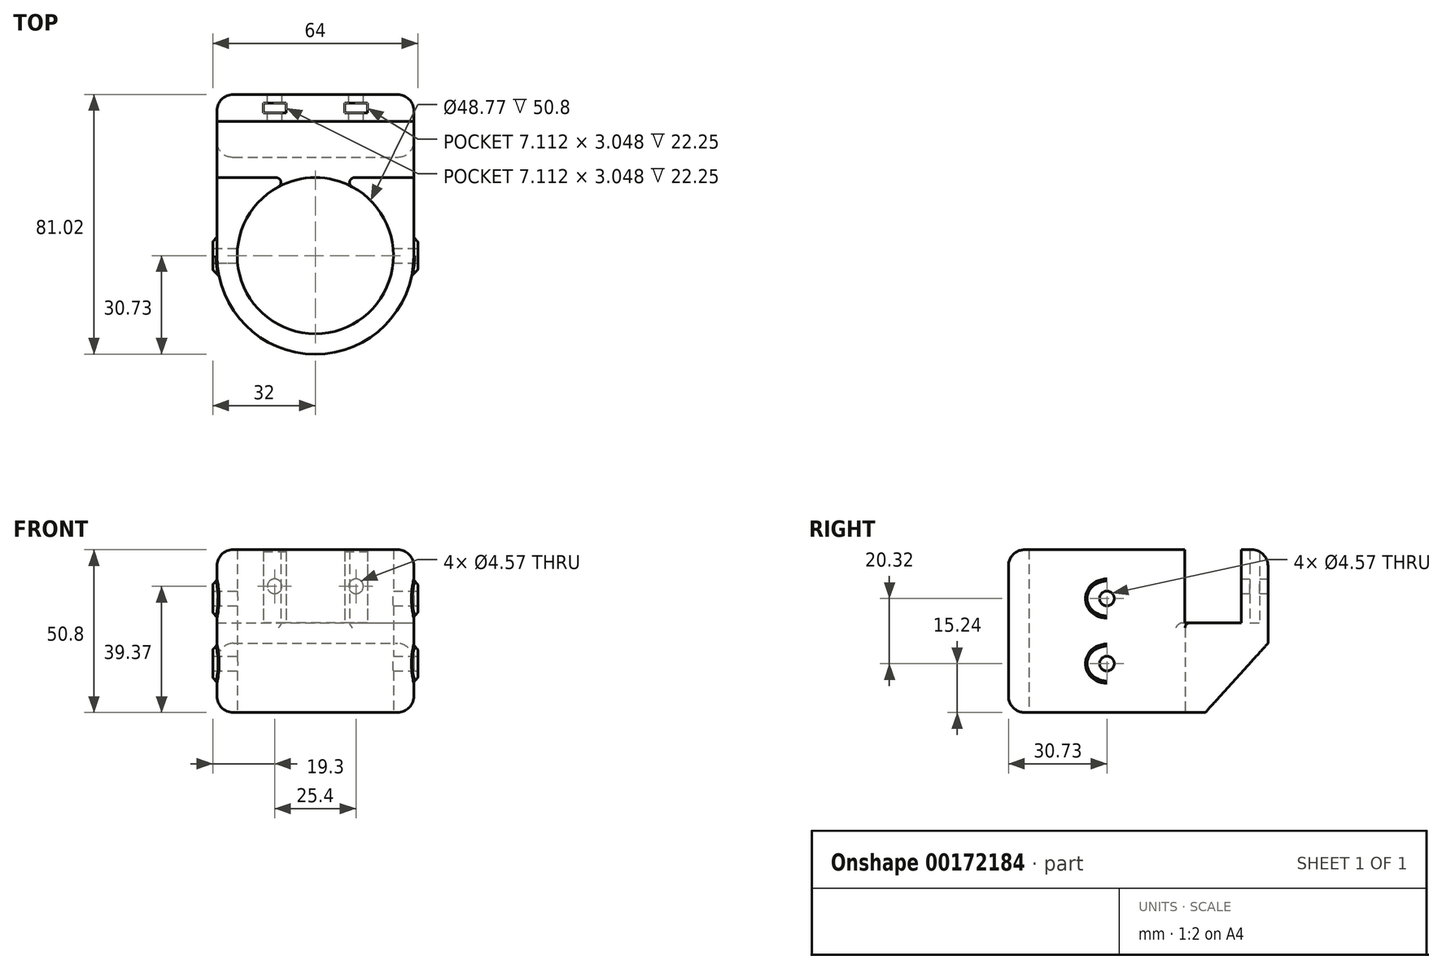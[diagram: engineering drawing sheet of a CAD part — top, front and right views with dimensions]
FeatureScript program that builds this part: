
annotation { "Feature Type Name" : "Feature", "Feature Type Description" : "" }
export const myFeature = defineFeature(function(context is Context, id is Id, definition is map)
    precondition{}
    {
        {
            var Q0;
            Q0=qCreatedBy(makeId("Top.planeOp"),FACE);
            var sketch = newSketch(context, id + "F0", { "sketchPlane" : qUnion([Q0])});
            skCircle(sketch, "E0", {"center": v(0, 0) * mm, "radius": 24.38 * mm});
            skArc(sketch, "E1", {"start": v(-30.73, 0) * mm, "mid": v(0, -30.73) * mm, "end": v(30.73, 0) * mm});
            skLineSegment(sketch, "E2", {"start": v(30.73, 0) * mm, "end": v(24.38, 0) * mm, "construction": true});
            skLineSegment(sketch, "E3.bottom", {"start": v(-30.73, 24.38) * mm, "end": v(30.73, 24.38) * mm, "construction": true});
            skLineSegment(sketch, "E3.top", {"start": v(-30.73, 41.9) * mm, "end": v(30.73, 41.9) * mm, "construction": true});
            skLineSegment(sketch, "E3.left", {"start": v(-30.73, 24.38) * mm, "end": v(-30.73, 41.9) * mm, "construction": true});
            skLineSegment(sketch, "E3.right", {"start": v(30.73, 24.38) * mm, "end": v(30.73, 41.9) * mm, "construction": true});
            skLineSegment(sketch, "E4", {"start": v(-30.73, 0) * mm, "end": v(-30.73, 50.3) * mm});
            skLineSegment(sketch, "E5", {"start": v(-30.73, 50.3) * mm, "end": v(30.73, 50.3) * mm});
            skLineSegment(sketch, "E6", {"start": v(30.73, 50.3) * mm, "end": v(30.73, 0) * mm});
            skSolve(sketch);
        }
        {
            var Q0;
            Q0 = qSketchRegion(id + "F0", true);
            extrude(context, id + "F1", {"entities" : qUnion([Q0]), "depth" : 50.8 * mm});
        }
        {
            var Q0;
            Q0=makeQuery(id+"F1.opExtrude","CAP_FACE",FACE,{"disambiguationData":[OSD([sQuery(id+"F0.wireOp",EDGE,"E0"),sQuery(id+"F0.wireOp",EDGE,"E1"),sQuery(id+"F0.wireOp",EDGE,"E4"),sQuery(id+"F0.wireOp",EDGE,"E5"),sQuery(id+"F0.wireOp",EDGE,"E6")])],"isStart":false});
            var sketch = newSketch(context, id + "F2", { "sketchPlane" : qUnion([Q0])});
            skLineSegment(sketch, "E7.bottom", {"start": v(-30.73, 41.9) * mm, "end": v(30.73, 41.9) * mm});
            skLineSegment(sketch, "E7.top", {"start": v(-30.73, 24.36) * mm, "end": v(30.73, 24.36) * mm});
            skLineSegment(sketch, "E7.left", {"start": v(-30.73, 41.9) * mm, "end": v(-30.73, 24.36) * mm});
            skLineSegment(sketch, "E7.right", {"start": v(30.73, 41.9) * mm, "end": v(30.73, 24.36) * mm});
            skLineSegment(sketch, "E8", {"start": v(0, 24.38) * mm, "end": v(0, 24.36) * mm, "construction": true});
            skSolve(sketch);
        }
        {
            var Q0;
            Q0 = qSketchRegion(id + "F2", true);
            extrude(context, id + "F3", {"entities" : qUnion([Q0]), "operationType" : NewBodyOperationType.REMOVE, "oppositeDirection" : true, "depth" : 22.86 * mm});
        }
        {
            var Q0;
            Q0=makeQuery(id+"F1.opExtrude","SWEPT_FACE",FACE,{"disambiguationData":[OSD([sQuery(id+"F0.wireOp",EDGE,"E6")])]});
            var sketch = newSketch(context, id + "F4", { "sketchPlane" : qUnion([Q0])});
            skLineSegment(sketch, "E9", {"start": v(50.3, 21.6) * mm, "end": v(30.73, 0) * mm});
            skLineSegment(sketch, "E10", {"start": v(30.73, 0) * mm, "end": v(50.3, 0) * mm});
            skLineSegment(sketch, "E11", {"start": v(50.3, 0) * mm, "end": v(50.3, 21.6) * mm});
            skSolve(sketch);
        }
        {
            var Q0;
            Q0 = qSketchRegion(id + "F4", true);
            var Q1;
            Q1=makeQuery(id+"F1.opExtrude","SWEPT_FACE",FACE,{"disambiguationData":[OSD([sQuery(id+"F0.wireOp",EDGE,"E4")])]});
            extrude(context, id + "F5", {"entities" : qUnion([Q0]), "operationType" : NewBodyOperationType.REMOVE, "endBound" : BoundingType.UP_TO_SURFACE, "oppositeDirection" : true, "endBoundEntityFace" : qUnion([Q1]), "depth" : 25.4 * mm});
        }
        {
            var Q0;
            Q0=makeQuery(id+"F1.opExtrude","SWEPT_EDGE",EDGE,{"disambiguationData":[OSD([sQuery(id+"F0.wireOp",EDGE,"E5"),sQuery(id+"F0.wireOp",EDGE,"E6")])]});
            var Q1;
            Q1=makeQuery(id+"F1.opExtrude","SWEPT_EDGE",EDGE,{"disambiguationData":[OSD([sQuery(id+"F0.wireOp",EDGE,"E4"),sQuery(id+"F0.wireOp",EDGE,"E5")])]});
            var Q2;
            Q2=makeQuery(id+"F5.boolean.opBoolean","COPY",EDGE,{"derivedFrom":makeQuery(id+"F5.opExtrude","CAP_EDGE",EDGE,{"disambiguationData":[OSD([sQuery(id+"F4.wireOp",EDGE,"E9")])],"isStart":true})});
            var Q3;
            Q3=makeQuery(id+"F5.boolean.opBoolean","COPY",EDGE,{"derivedFrom":makeQuery(id+"F5.opExtrude","SWEPT_EDGE",EDGE,{"disambiguationData":[OSD([sQuery(id+"F0.wireOp",EDGE,"E5"),sQuery(id+"F0.wireOp",EDGE,"E6"),sQuery(id+"F4.wireOp",EDGE,"E9"),sQuery(id+"F4.wireOp",EDGE,"E11")])]})});
            var Q4;
            Q4=makeQuery(id+"F5.boolean.opBoolean","COPY",EDGE,{"derivedFrom":makeQuery(id+"F5.opExtrude","CAP_EDGE",EDGE,{"disambiguationData":[OSD([sQuery(id+"F4.wireOp",EDGE,"E9")])],"isStart":false})});
            var Q5;
            Q5=makeQuery(id+"F1.opExtrude","CAP_EDGE",EDGE,{"disambiguationData":[OSD([sQuery(id+"F0.wireOp",EDGE,"E1")])],"isStart":true});
            var Q6;
            Q6=makeQuery(id+"F5.boolean.opBoolean","COPY",EDGE,{"derivedFrom":makeQuery(id+"F5.opExtrude","SWEPT_EDGE",EDGE,{"disambiguationData":[OSD([sQuery(id+"F0.wireOp",EDGE,"E6"),sQuery(id+"F4.wireOp",EDGE,"E9"),sQuery(id+"F4.wireOp",EDGE,"E10")])]})});
            var Q7;
            Q7=makeQuery(id+"F1.opExtrude","CAP_EDGE",EDGE,{"disambiguationData":[OSD([sQuery(id+"F0.wireOp",EDGE,"E1")])],"isStart":false});
            var Q8;
            Q8=makeQuery(id+"F1.opExtrude","CAP_EDGE",EDGE,{"disambiguationData":[OSD([sQuery(id+"F0.wireOp",EDGE,"E5")])],"isStart":false});
            var Q9;
            {var subQ0=sQuery(id+"F0.wireOp",EDGE,"E6");var subQ1=sQuery(id+"F0.wireOp",EDGE,"E5");Q9=makeQuery(id+"F3.boolean.opBoolean","SPLIT",EDGE,{"disambiguationData":[TD([makeQuery(id+"F1.opExtrude","SWEPT_FACE",FACE,{"disambiguationData":[OSD([subQ1])]})])],"derivedFrom":makeQuery(id+"F1.opExtrude","CAP_EDGE",EDGE,{"disambiguationData":[OSD([subQ0])],"isStart":false})});}
            var Q10;
            {var subQ0=sQuery(id+"F0.wireOp",EDGE,"E5");var subQ1=sQuery(id+"F0.wireOp",EDGE,"E4");Q10=makeQuery(id+"F3.boolean.opBoolean","SPLIT",EDGE,{"disambiguationData":[TD([makeQuery(id+"F1.opExtrude","SWEPT_FACE",FACE,{"disambiguationData":[OSD([subQ0])]})])],"derivedFrom":makeQuery(id+"F1.opExtrude","CAP_EDGE",EDGE,{"disambiguationData":[OSD([subQ1])],"isStart":false})});}
            fillet(context, id + "F6", {"entities" : qUnion([Q0, Q1, Q2, Q3, Q4, Q5, Q6, Q7, Q8, Q9, Q10]), "radius" : 5.08 * mm, "tangentPropagation" : true, "allowEdgeOverflow" : false});
        }
        {
            var Q0;
            Q0=makeQuery(id+"F3.boolean.opBoolean","COPY",EDGE,{"derivedFrom":makeQuery(id+"F3.opExtrude","SWEPT_EDGE",EDGE,{"disambiguationData":[OSD([sQuery(id+"F0.wireOp",EDGE,"E6"),sQuery(id+"F2.wireOp",EDGE,"E7.top"),sQuery(id+"F2.wireOp",EDGE,"E7.right")])]})});
            var Q1;
            Q1=makeQuery(id+"F3.boolean.opBoolean","COPY",EDGE,{"derivedFrom":makeQuery(id+"F3.opExtrude","SWEPT_EDGE",EDGE,{"disambiguationData":[OSD([sQuery(id+"F0.wireOp",EDGE,"E6"),sQuery(id+"F2.wireOp",EDGE,"E7.bottom"),sQuery(id+"F2.wireOp",EDGE,"E7.right")])]})});
            var Q2;
            Q2=makeQuery(id+"F3.boolean.opBoolean","COPY",EDGE,{"derivedFrom":makeQuery(id+"F3.opExtrude","CAP_EDGE",EDGE,{"disambiguationData":[OSD([sQuery(id+"F2.wireOp",EDGE,"E7.right")])],"isStart":false})});
            var Q3;
            Q3=makeQuery(id+"F3.boolean.opBoolean","COPY",EDGE,{"derivedFrom":makeQuery(id+"F3.opExtrude","CAP_EDGE",EDGE,{"disambiguationData":[OSD([sQuery(id+"F2.wireOp",EDGE,"E7.left")])],"isStart":false})});
            var Q4;
            Q4=makeQuery(id+"F3.boolean.opBoolean","COPY",EDGE,{"derivedFrom":makeQuery(id+"F3.opExtrude","SWEPT_EDGE",EDGE,{"disambiguationData":[OSD([sQuery(id+"F0.wireOp",EDGE,"E4"),sQuery(id+"F2.wireOp",EDGE,"E7.top"),sQuery(id+"F2.wireOp",EDGE,"E7.left")])]})});
            var Q5;
            Q5=makeQuery(id+"F3.boolean.opBoolean","COPY",EDGE,{"derivedFrom":makeQuery(id+"F3.opExtrude","SWEPT_EDGE",EDGE,{"disambiguationData":[OSD([sQuery(id+"F0.wireOp",EDGE,"E4"),sQuery(id+"F2.wireOp",EDGE,"E7.bottom"),sQuery(id+"F2.wireOp",EDGE,"E7.left")])]})});
            var Q6;
            Q6=makeQuery(id+"F3.boolean.opBoolean","INTERSECT",EDGE,{"derivedFrom":[makeQuery(id+"F1.opExtrude","SWEPT_FACE",FACE,{"disambiguationData":[OSD([sQuery(id+"F0.wireOp",EDGE,"E0")])]}),makeQuery(id+"F3.opExtrude","CAP_FACE",FACE,{"disambiguationData":[OSD([sQuery(id+"F2.wireOp",EDGE,"E7.bottom"),sQuery(id+"F2.wireOp",EDGE,"E7.top"),sQuery(id+"F2.wireOp",EDGE,"E7.left"),sQuery(id+"F2.wireOp",EDGE,"E7.right")])],"isStart":false})]});
            var Q7;
            Q7=makeQuery(id+"F3.boolean.opBoolean","INTERSECT",EDGE,{"disambiguationData":[OD(0.0)],"derivedFrom":[makeQuery(id+"F1.opExtrude","SWEPT_FACE",FACE,{"disambiguationData":[OSD([sQuery(id+"F0.wireOp",EDGE,"E0")])]}),makeQuery(id+"F3.opExtrude","SWEPT_FACE",FACE,{"disambiguationData":[OSD([sQuery(id+"F2.wireOp",EDGE,"E7.top")])]})]});
            var Q8;
            Q8=makeQuery(id+"F3.boolean.opBoolean","INTERSECT",EDGE,{"disambiguationData":[OD(1.0)],"derivedFrom":[makeQuery(id+"F1.opExtrude","SWEPT_FACE",FACE,{"disambiguationData":[OSD([sQuery(id+"F0.wireOp",EDGE,"E0")])]}),makeQuery(id+"F3.opExtrude","SWEPT_FACE",FACE,{"disambiguationData":[OSD([sQuery(id+"F2.wireOp",EDGE,"E7.top")])]})]});
            fillet(context, id + "F7", {"entities" : qUnion([Q0, Q1, Q2, Q3, Q4, Q5, Q6, Q7, Q8]), "radius" : 1.52 * mm, "tangentPropagation" : true, "allowEdgeOverflow" : false});
        }
        {
            var Q0;
            Q0=makeQuery(id+"F1.opExtrude","SWEPT_FACE",FACE,{"disambiguationData":[OSD([sQuery(id+"F0.wireOp",EDGE,"E6")])]});
            var sketch = newSketch(context, id + "F8", { "sketchPlane" : qUnion([Q0])});
            skCircle(sketch, "E12", {"center": v(0, 35.56) * mm, "radius": 6.35 * mm});
            skCircle(sketch, "E13", {"center": v(0, 15.24) * mm, "radius": 6.35 * mm});
            skLineSegment(sketch, "E14", {"start": v(0, 41.91) * mm, "end": v(0, 45.72) * mm, "construction": true});
            skLineSegment(sketch, "E15", {"start": v(0, 8.9) * mm, "end": v(0, 5.08) * mm, "construction": true});
            skSolve(sketch);
        }
        {
            var Q0;
            Q0=makeQuery(id+"F1.opExtrude","SWEPT_FACE",FACE,{"disambiguationData":[OSD([sQuery(id+"F0.wireOp",EDGE,"E4")])]});
            var sketch = newSketch(context, id + "F9", { "sketchPlane" : qUnion([Q0])});
            skCircle(sketch, "E16", {"center": v(0, 35.56) * mm, "radius": 6.35 * mm});
            skCircle(sketch, "E17", {"center": v(0, 15.24) * mm, "radius": 6.35 * mm});
            skSolve(sketch);
        }
        {
            var Q0;
            Q0 = qSketchRegion(id + "F8", true);
            var Q1;
            Q1 = qSketchRegion(id + "F9", true);
            extrude(context, id + "F10", {"entities" : qUnion([Q0, Q1]), "operationType" : NewBodyOperationType.ADD, "endBound" : BoundingType.SYMMETRIC, "depth" : 2.54 * mm});
        }
        {
            var Q0;
            Q0=makeQuery(id+"F10.opExtrude","CAP_EDGE",EDGE,{"disambiguationData":[OSD([sQuery(id+"F8.wireOp",EDGE,"E12")])],"isStart":false});
            var Q1;
            Q1=makeQuery(id+"F10.opExtrude","CAP_EDGE",EDGE,{"disambiguationData":[OSD([sQuery(id+"F8.wireOp",EDGE,"E13")])],"isStart":false});
            var Q2;
            Q2=makeQuery(id+"F10.opExtrude","CAP_EDGE",EDGE,{"disambiguationData":[OSD([sQuery(id+"F9.wireOp",EDGE,"E16")])],"isStart":true});
            var Q3;
            Q3=makeQuery(id+"F10.opExtrude","CAP_EDGE",EDGE,{"disambiguationData":[OSD([sQuery(id+"F9.wireOp",EDGE,"E17")])],"isStart":true});
            chamfer(context, id + "F11", {"entities" : qUnion([Q0, Q1, Q2, Q3]), "width" : 1.9 * mm, "tangentPropagation" : true});
        }
        {
            var Q0;
            {var subQ0=sQuery(id+"F8.wireOp",EDGE,"E12");Q0=makeQuery(id+"F11.opChamfer","BLEND_EDGE",EDGE,{"blendedFrom":[makeQuery(id+"F10.opExtrude","CAP_EDGE",EDGE,{"disambiguationData":[OSD([subQ0])],"isStart":false}),makeQuery(id+"F10.opExtrude","CAP_FACE",FACE,{"disambiguationData":[OSD([subQ0])],"isStart":false})],"blendedInto":[makeQuery(id+"F10.opExtrude","CAP_FACE",FACE,{"disambiguationData":[OSD([subQ0])],"isStart":false})]});}
            var Q1;
            {var subQ0=sQuery(id+"F8.wireOp",EDGE,"E13");Q1=makeQuery(id+"F11.opChamfer","BLEND_EDGE",EDGE,{"blendedFrom":[makeQuery(id+"F10.opExtrude","CAP_EDGE",EDGE,{"disambiguationData":[OSD([subQ0])],"isStart":false}),makeQuery(id+"F10.opExtrude","CAP_FACE",FACE,{"disambiguationData":[OSD([subQ0])],"isStart":false})],"blendedInto":[makeQuery(id+"F10.opExtrude","CAP_FACE",FACE,{"disambiguationData":[OSD([subQ0])],"isStart":false})]});}
            var Q2;
            Q2=makeQuery(id+"F11.opChamfer","BLEND_EDGE",EDGE,{"disambiguationData":[OD(1.0)],"blendedFrom":[makeQuery(id+"F10.opExtrude","CAP_EDGE",EDGE,{"disambiguationData":[OSD([sQuery(id+"F8.wireOp",EDGE,"E12")])],"isStart":false}),makeQuery(id+"F1.opExtrude","SWEPT_FACE",FACE,{"disambiguationData":[OSD([sQuery(id+"F0.wireOp",EDGE,"E1")])]})],"blendedInto":[makeQuery(id+"F1.opExtrude","SWEPT_FACE",FACE,{"disambiguationData":[OSD([sQuery(id+"F0.wireOp",EDGE,"E1")])]})]});
            var Q3;
            Q3=makeQuery(id+"F11.opChamfer","BLEND_EDGE",EDGE,{"disambiguationData":[OD(1.0)],"blendedFrom":[makeQuery(id+"F10.opExtrude","CAP_EDGE",EDGE,{"disambiguationData":[OSD([sQuery(id+"F8.wireOp",EDGE,"E13")])],"isStart":false}),makeQuery(id+"F1.opExtrude","SWEPT_FACE",FACE,{"disambiguationData":[OSD([sQuery(id+"F0.wireOp",EDGE,"E1")])]})],"blendedInto":[makeQuery(id+"F1.opExtrude","SWEPT_FACE",FACE,{"disambiguationData":[OSD([sQuery(id+"F0.wireOp",EDGE,"E1")])]})]});
            var Q4;
            Q4=makeQuery(id+"F11.opChamfer","BLEND_EDGE",EDGE,{"disambiguationData":[OD(1.0)],"blendedFrom":[makeQuery(id+"F10.opExtrude","CAP_EDGE",EDGE,{"disambiguationData":[OSD([sQuery(id+"F9.wireOp",EDGE,"E16")])],"isStart":true}),makeQuery(id+"F1.opExtrude","SWEPT_FACE",FACE,{"disambiguationData":[OSD([sQuery(id+"F0.wireOp",EDGE,"E1")])]})],"blendedInto":[makeQuery(id+"F1.opExtrude","SWEPT_FACE",FACE,{"disambiguationData":[OSD([sQuery(id+"F0.wireOp",EDGE,"E1")])]})]});
            var Q5;
            Q5=makeQuery(id+"F11.opChamfer","BLEND_EDGE",EDGE,{"disambiguationData":[OD(1.0)],"blendedFrom":[makeQuery(id+"F10.opExtrude","CAP_EDGE",EDGE,{"disambiguationData":[OSD([sQuery(id+"F9.wireOp",EDGE,"E17")])],"isStart":true}),makeQuery(id+"F1.opExtrude","SWEPT_FACE",FACE,{"disambiguationData":[OSD([sQuery(id+"F0.wireOp",EDGE,"E1")])]})],"blendedInto":[makeQuery(id+"F1.opExtrude","SWEPT_FACE",FACE,{"disambiguationData":[OSD([sQuery(id+"F0.wireOp",EDGE,"E1")])]})]});
            var Q6;
            {var subQ0=sQuery(id+"F9.wireOp",EDGE,"E17");Q6=makeQuery(id+"F11.opChamfer","BLEND_EDGE",EDGE,{"blendedFrom":[makeQuery(id+"F10.opExtrude","CAP_EDGE",EDGE,{"disambiguationData":[OSD([subQ0])],"isStart":true}),makeQuery(id+"F10.opExtrude","CAP_FACE",FACE,{"disambiguationData":[OSD([subQ0])],"isStart":true})],"blendedInto":[makeQuery(id+"F10.opExtrude","CAP_FACE",FACE,{"disambiguationData":[OSD([subQ0])],"isStart":true})]});}
            var Q7;
            {var subQ0=sQuery(id+"F9.wireOp",EDGE,"E16");Q7=makeQuery(id+"F11.opChamfer","BLEND_EDGE",EDGE,{"blendedFrom":[makeQuery(id+"F10.opExtrude","CAP_EDGE",EDGE,{"disambiguationData":[OSD([subQ0])],"isStart":true}),makeQuery(id+"F10.opExtrude","CAP_FACE",FACE,{"disambiguationData":[OSD([subQ0])],"isStart":true})],"blendedInto":[makeQuery(id+"F10.opExtrude","CAP_FACE",FACE,{"disambiguationData":[OSD([subQ0])],"isStart":true})]});}
            fillet(context, id + "F12", {"entities" : qUnion([Q0, Q1, Q2, Q3, Q4, Q5, Q6, Q7]), "radius" : 1.02 * mm, "tangentPropagation" : true, "allowEdgeOverflow" : false});
        }
        {
            var Q0;
            Q0=qCreatedBy(makeId("Right.planeOp"),FACE);
            var sketch = newSketch(context, id + "F13", { "sketchPlane" : qUnion([Q0])});
            skCircle(sketch, "E18", {"center": v(0, 35.56) * mm, "radius": 2.29 * mm});
            skCircle(sketch, "E19", {"center": v(0, 15.24) * mm, "radius": 2.29 * mm});
            skSolve(sketch);
        }
        {
            var Q0;
            Q0 = qSketchRegion(id + "F13", true);
            extrude(context, id + "F14", {"entities" : qUnion([Q0]), "operationType" : NewBodyOperationType.REMOVE, "endBound" : BoundingType.THROUGH_ALL, "oppositeDirection" : true, "depth" : 25.4 * mm, "hasSecondDirection" : true, "secondDirectionBound" : SecondDirectionBoundingType.THROUGH_ALL, "secondDirectionOppositeDirection" : false, "secondDirectionDepth" : 25.4 * mm});
        }
        {
            var Q0;
            Q0=makeQuery(id+"F1.opExtrude","SWEPT_FACE",FACE,{"disambiguationData":[OSD([sQuery(id+"F0.wireOp",EDGE,"E5")])]});
            var sketch = newSketch(context, id + "F15", { "sketchPlane" : qUnion([Q0])});
            skLineSegment(sketch, "E20", {"start": v(0, 50.8) * mm, "end": v(0, 27.94) * mm, "construction": true});
            skCircle(sketch, "E21", {"center": v(-12.7, 39.37) * mm, "radius": 2.29 * mm});
            skCircle(sketch, "E22", {"center": v(12.7, 39.37) * mm, "radius": 2.29 * mm});
            skPoint(sketch, "E23", {"position": v(0, 39.37) * mm});
            skLineSegment(sketch, "E24", {"start": v(-12.7, 39.37) * mm, "end": v(12.7, 39.37) * mm, "construction": true});
            skSolve(sketch);
        }
        {
            var Q0;
            Q0 = qSketchRegion(id + "F15", true);
            var Q1;
            Q1=makeQuery(id+"F3.boolean.opBoolean","COPY",FACE,{"derivedFrom":makeQuery(id+"F3.opExtrude","SWEPT_FACE",FACE,{"disambiguationData":[OSD([sQuery(id+"F2.wireOp",EDGE,"E7.bottom")])]})});
            extrude(context, id + "F16", {"entities" : qUnion([Q0]), "operationType" : NewBodyOperationType.REMOVE, "endBound" : BoundingType.UP_TO_SURFACE, "oppositeDirection" : true, "endBoundEntityFace" : qUnion([Q1]), "depth" : 25.4 * mm});
        }
        {
            var Q0;
            Q0=makeQuery(id+"F3.boolean.opBoolean","COPY",FACE,{"derivedFrom":makeQuery(id+"F3.opExtrude","CAP_FACE",FACE,{"disambiguationData":[OSD([sQuery(id+"F2.wireOp",EDGE,"E7.bottom"),sQuery(id+"F2.wireOp",EDGE,"E7.top"),sQuery(id+"F2.wireOp",EDGE,"E7.left"),sQuery(id+"F2.wireOp",EDGE,"E7.right")])],"isStart":false})});
            var sketch = newSketch(context, id + "F17", { "sketchPlane" : qUnion([Q0])});
            skLineSegment(sketch, "E25.bottom", {"start": v(16.26, 44.58) * mm, "end": v(9.14, 44.58) * mm});
            skLineSegment(sketch, "E25.top", {"start": v(16.26, 47.62) * mm, "end": v(9.14, 47.62) * mm});
            skLineSegment(sketch, "E25.left", {"start": v(16.26, 44.58) * mm, "end": v(16.26, 47.62) * mm});
            skLineSegment(sketch, "E25.right", {"start": v(9.14, 44.58) * mm, "end": v(9.14, 47.62) * mm});
            skLineSegment(sketch, "E26.bottom", {"start": v(-9.14, 44.58) * mm, "end": v(-16.26, 44.58) * mm});
            skLineSegment(sketch, "E26.top", {"start": v(-9.14, 47.62) * mm, "end": v(-16.26, 47.62) * mm});
            skLineSegment(sketch, "E26.left", {"start": v(-9.14, 44.58) * mm, "end": v(-9.14, 47.62) * mm});
            skLineSegment(sketch, "E26.right", {"start": v(-16.26, 44.58) * mm, "end": v(-16.26, 47.62) * mm});
            skPoint(sketch, "E27", {"position": v(12.7, 44.58) * mm});
            skPoint(sketch, "E28", {"position": v(-12.7, 44.58) * mm});
            skLineSegment(sketch, "E29", {"start": v(0, 41.9) * mm, "end": v(0, 50.3) * mm, "construction": true});
            skPoint(sketch, "E29.endSnap0", {"position": v(0, 41.9) * mm});
            skPoint(sketch, "E30", {"position": v(0, 46.1) * mm});
            skPoint(sketch, "E31", {"position": v(9.14, 46.1) * mm});
            skSolve(sketch);
        }
        {
            var Q0;
            Q0 = qSketchRegion(id + "F17", true);
            var Q1;
            {var subQ0=sQuery(id+"F0.wireOp",EDGE,"E4");var subQ1=sQuery(id+"F0.wireOp",EDGE,"E5");var subQ2=sQuery(id+"F0.wireOp",EDGE,"E6");Q1=makeQuery(id+"F3.boolean.opBoolean","SPLIT",FACE,{"disambiguationData":[TD([makeQuery(id+"F1.opExtrude","SWEPT_FACE",FACE,{"disambiguationData":[OSD([subQ1])]})])],"derivedFrom":makeQuery(id+"F1.opExtrude","CAP_FACE",FACE,{"disambiguationData":[OSD([sQuery(id+"F0.wireOp",EDGE,"E0"),sQuery(id+"F0.wireOp",EDGE,"E1"),subQ0,subQ1,subQ2])],"isStart":false})});}
            extrude(context, id + "F18", {"entities" : qUnion([Q0]), "operationType" : NewBodyOperationType.REMOVE, "endBound" : BoundingType.UP_TO_SURFACE, "endBoundEntityFace" : qUnion([Q1]), "depth" : 25.4 * mm});
        }
    });
